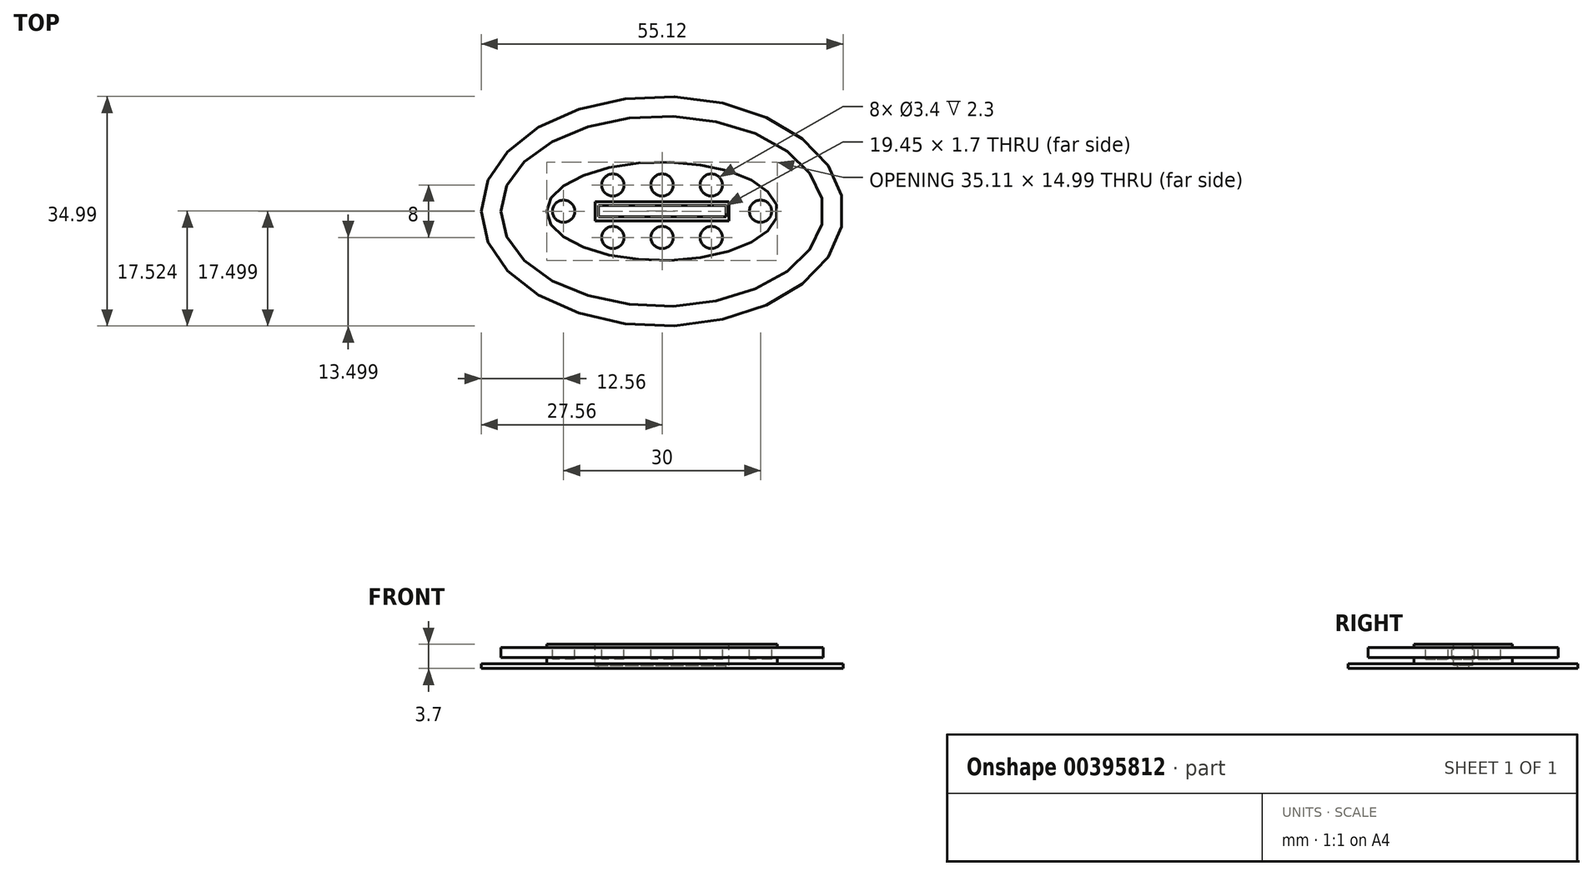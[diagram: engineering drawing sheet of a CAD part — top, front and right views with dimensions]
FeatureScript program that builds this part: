
annotation { "Feature Type Name" : "Feature", "Feature Type Description" : "" }
export const myFeature = defineFeature(function(context is Context, id is Id, definition is map)
    precondition{}
    {
        {
            var Q0;
            Q0=qCreatedBy(makeId("Top.planeOp"),FACE);
            var sketch = newSketch(context, id + "F0", { "sketchPlane" : qUnion([Q0])});
            skPoint(sketch, "E0", {"position": v(0, 39.46) * mm});
            skEllipse(sketch, "E1", {"center": v(0, 39.46) * mm, "majorRadius": 17.56 * mm, "minorRadius": 7.5 * mm, "majorAxis": v(-1, 0)});
            skSolve(sketch);
        }
        {
            var Q0;
            Q0 = qSketchRegion(id + "F0", true);
            var Q1;
            Q1 = qSketchRegion(id + "F2", true);
            extrude(context, id + "F1", {"entities" : qUnion([Q0, Q1]), "oppositeDirection" : true, "offsetDistance" : 25 * mm, "depth" : 2 * mm});
        }
        {
            var Q0;
            Q0=makeQuery(id+"F1.opExtrude","CAP_FACE",FACE,{"disambiguationData":[OSD([sQuery(id+"F0.wireOp",EDGE,"E1")])],"isStart":true});
            var sketch = newSketch(context, id + "F2", { "sketchPlane" : qUnion([Q0])});
            skPoint(sketch, "E2", {"position": v(0, 39.46) * mm});
            skEllipse(sketch, "E3", {"center": v(0, 39.46) * mm, "majorRadius": 24.56 * mm, "minorRadius": 14.5 * mm, "majorAxis": v(-1, 0)});
            skPoint(sketch, "E4", {"position": v(-24.56, 39.46) * mm});
            skPoint(sketch, "E5", {"position": v(0, 53.95) * mm});
            skPoint(sketch, "E6", {"position": v(0, 24.96) * mm});
            skPoint(sketch, "E7", {"position": v(24.56, 39.46) * mm});
            skPoint(sketch, "E8", {"position": v(0, 46.95) * mm});
            skPoint(sketch, "E9", {"position": v(-17.56, 39.46) * mm});
            skPoint(sketch, "E10", {"position": v(0, 31.96) * mm});
            skPoint(sketch, "E11", {"position": v(17.56, 39.46) * mm});
            skSolve(sketch);
        }
        {
            var Q0;
            Q0 = qSketchRegion(id + "F2", true);
            extrude(context, id + "F3", {"entities" : qUnion([Q0]), "operationType" : NewBodyOperationType.ADD, "oppositeDirection" : true, "depth" : 0.5 * mm});
        }
        {
            var Q0;
            Q0=makeQuery(id+"F3.boolean.opBoolean","MERGE",FACE,{"derivedFrom":[makeQuery(id+"F1.opExtrude","CAP_FACE",FACE,{"disambiguationData":[OSD([sQuery(id+"F0.wireOp",EDGE,"E1")])],"isStart":true}),makeQuery(id+"F3.opExtrude","CAP_FACE",FACE,{"disambiguationData":[OSD([sQuery(id+"F2.wireOp",EDGE,"E3")])],"isStart":true})]});
            var sketch = newSketch(context, id + "F4", { "sketchPlane" : qUnion([Q0])});
            skPoint(sketch, "E12", {"position": v(0, 39.46) * mm});
            skEllipse(sketch, "E13", {"center": v(0, 39.46) * mm, "majorRadius": 17.56 * mm, "minorRadius": 7.5 * mm, "majorAxis": v(-1, 0)});
            skSolve(sketch);
        }
        {
            var Q0;
            Q0 = qSketchRegion(id + "F4", true);
            extrude(context, id + "F5", {"entities" : qUnion([Q0]), "operationType" : NewBodyOperationType.ADD, "depth" : 1.5 * mm});
        }
        {
            var Q0;
            Q0=makeQuery(id+"F5.opExtrude","CAP_FACE",FACE,{"disambiguationData":[OSD([sQuery(id+"F4.wireOp",EDGE,"E13")])],"isStart":false});
            var sketch = newSketch(context, id + "F6", { "sketchPlane" : qUnion([Q0])});
            skPoint(sketch, "E14", {"position": v(0, 39.46) * mm});
            skLineSegment(sketch, "E15.bottom", {"start": v(-10.2, 40.9) * mm, "end": v(10.2, 40.9) * mm});
            skLineSegment(sketch, "E15.top", {"start": v(-10.2, 38) * mm, "end": v(10.2, 38) * mm});
            skLineSegment(sketch, "E15.left", {"start": v(-10.2, 40.9) * mm, "end": v(-10.2, 38) * mm});
            skLineSegment(sketch, "E15.right", {"start": v(10.2, 40.9) * mm, "end": v(10.2, 38) * mm});
            skSolve(sketch);
        }
        {
            var Q0;
            Q0=makeQuery(id+"F5.opExtrude","CAP_FACE",FACE,{"disambiguationData":[OSD([sQuery(id+"F4.wireOp",EDGE,"E13")])],"isStart":false});
            var sketch = newSketch(context, id + "F7", { "sketchPlane" : qUnion([Q0])});
            skPoint(sketch, "E16", {"position": v(0, 39.46) * mm});
            skPoint(sketch, "E17", {"position": v(-15, 39.46) * mm});
            skPoint(sketch, "E18", {"position": v(0, 43.46) * mm});
            skPoint(sketch, "E19", {"position": v(0, 35.46) * mm});
            skPoint(sketch, "E20", {"position": v(15, 39.46) * mm});
            skCircle(sketch, "E21", {"center": v(-15, 39.46) * mm, "radius": 1.7 * mm});
            skCircle(sketch, "E22", {"center": v(0, 43.46) * mm, "radius": 1.7 * mm});
            skCircle(sketch, "E23", {"center": v(15, 39.46) * mm, "radius": 1.7 * mm});
            skCircle(sketch, "E24", {"center": v(0, 35.46) * mm, "radius": 1.7 * mm});
            skPoint(sketch, "E25", {"position": v(-7.5, 43.46) * mm});
            skPoint(sketch, "E26", {"position": v(7.5, 43.46) * mm});
            skPoint(sketch, "E27", {"position": v(7.5, 35.46) * mm});
            skPoint(sketch, "E28", {"position": v(-7.5, 35.46) * mm});
            skCircle(sketch, "E29", {"center": v(-7.5, 35.46) * mm, "radius": 1.7 * mm});
            skCircle(sketch, "E30", {"center": v(-7.5, 43.46) * mm, "radius": 1.7 * mm});
            skCircle(sketch, "E31", {"center": v(7.5, 43.46) * mm, "radius": 1.7 * mm});
            skCircle(sketch, "E32", {"center": v(7.5, 35.46) * mm, "radius": 1.7 * mm});
            skSolve(sketch);
        }
        {
            var Q0;
            Q0 = qSketchRegion(id + "F7", true);
            extrude(context, id + "F8", {"entities" : qUnion([Q0]), "operationType" : NewBodyOperationType.REMOVE, "oppositeDirection" : true, "depth" : 2.3 * mm});
        }
        {
            var Q0;
            Q0=makeQuery(id+"F1.opExtrude","CAP_FACE",FACE,{"disambiguationData":[OSD([sQuery(id+"F0.wireOp",EDGE,"E1")])],"isStart":false});
            var sketch = newSketch(context, id + "F9", { "sketchPlane" : qUnion([Q0])});
            skPoint(sketch, "E33", {"position": v(0, -39.46) * mm});
            skEllipse(sketch, "E34", {"center": v(0, -39.46) * mm, "majorRadius": 27.56 * mm, "minorRadius": 17.5 * mm, "majorAxis": v(-1, 0)});
            skPoint(sketch, "E35", {"position": v(-17.56, -39.46) * mm});
            skPoint(sketch, "E36", {"position": v(0, -31.96) * mm});
            skPoint(sketch, "E37.positionSnap0", {"position": v(17.56, -39.46) * mm});
            skPoint(sketch, "E38", {"position": v(0, -46.95) * mm});
            skPoint(sketch, "E39", {"position": v(-27.56, -39.46) * mm});
            skPoint(sketch, "E40", {"position": v(0, -21.96) * mm});
            skPoint(sketch, "E41", {"position": v(27.56, -39.46) * mm});
            skPoint(sketch, "E42", {"position": v(0, -56.95) * mm});
            skSolve(sketch);
        }
        {
            var Q0;
            Q0 = qSketchRegion(id + "F9", true);
            extrude(context, id + "F10", {"entities" : qUnion([Q0]), "operationType" : NewBodyOperationType.ADD, "oppositeDirection" : true, "depth" : 0.5 * mm});
        }
        {
            var Q0;
            Q0=makeQuery(id+"F10.boolean.opBoolean","MERGE",FACE,{"derivedFrom":[makeQuery(id+"F1.opExtrude","CAP_FACE",FACE,{"disambiguationData":[OSD([sQuery(id+"F0.wireOp",EDGE,"E1")])],"isStart":false}),makeQuery(id+"F10.opExtrude","CAP_FACE",FACE,{"disambiguationData":[OSD([sQuery(id+"F9.wireOp",EDGE,"E34")])],"isStart":true})]});
            var sketch = newSketch(context, id + "F11", { "sketchPlane" : qUnion([Q0])});
            skPoint(sketch, "E43", {"position": v(0, -39.46) * mm});
            skPoint(sketch, "E44", {"position": v(0, -56.95) * mm});
            skPoint(sketch, "E45", {"position": v(-27.56, -39.46) * mm});
            skPoint(sketch, "E46", {"position": v(0, -21.96) * mm});
            skPoint(sketch, "E47", {"position": v(27.56, -39.46) * mm});
            skEllipse(sketch, "E48", {"center": v(0, -39.46) * mm, "majorRadius": 17.56 * mm, "minorRadius": 7.5 * mm, "majorAxis": v(-1, 0)});
            skPoint(sketch, "E49", {"position": v(-17.56, -39.46) * mm});
            skPoint(sketch, "E50", {"position": v(0, -31.96) * mm});
            skPoint(sketch, "E51", {"position": v(17.56, -39.46) * mm});
            skPoint(sketch, "E52", {"position": v(0, -46.95) * mm});
            skSolve(sketch);
        }
        {
            var Q0;
            Q0 = qSketchRegion(id + "F11", true);
            extrude(context, id + "F12", {"entities" : qUnion([Q0]), "operationType" : NewBodyOperationType.ADD, "depth" : 0.2 * mm});
        }
        {
            var Q0;
            Q0=makeQuery(id+"F6.imprint","IMPRINT",FACE,{"disambiguationData":[TD([[makeQuery(id+"F6.imprint","IMPRINT",EDGE,{"derivedFrom":sQuery(id+"F6.wireOp",EDGE,"E15.bottom")}),-1.0]])]});
            extrude(context, id + "F13", {"entities" : qUnion([Q0]), "operationType" : NewBodyOperationType.REMOVE, "oppositeDirection" : true, "depth" : 3.2 * mm});
        }
        {
            var Q0;
            Q0=makeQuery(id+"F13.boolean.opBoolean","COPY",FACE,{"derivedFrom":makeQuery(id+"F13.opExtrude","CAP_FACE",FACE,{"disambiguationData":[OSD([sQuery(id+"F6.wireOp",EDGE,"E15.bottom"),sQuery(id+"F6.wireOp",EDGE,"E15.top"),sQuery(id+"F6.wireOp",EDGE,"E15.left"),sQuery(id+"F6.wireOp",EDGE,"E15.right")])],"isStart":false})});
            var sketch = newSketch(context, id + "F14", { "sketchPlane" : qUnion([Q0])});
            skPoint(sketch, "E53", {"position": v(0, 39.48) * mm});
            skPoint(sketch, "E54", {"position": v(0, 40.9) * mm});
            skPoint(sketch, "E55", {"position": v(0, 38) * mm});
            skPoint(sketch, "E56", {"position": v(10.2, 39.48) * mm});
            skPoint(sketch, "E57", {"position": v(-10.2, 39.48) * mm});
            skLineSegment(sketch, "E58.bottom", {"start": v(-9.72, 40.33) * mm, "end": v(9.72, 40.33) * mm});
            skLineSegment(sketch, "E58.top", {"start": v(-9.72, 38.63) * mm, "end": v(9.72, 38.63) * mm});
            skLineSegment(sketch, "E58.left", {"start": v(-9.72, 40.33) * mm, "end": v(-9.72, 38.63) * mm});
            skLineSegment(sketch, "E58.right", {"start": v(9.72, 40.33) * mm, "end": v(9.72, 38.63) * mm});
            skSolve(sketch);
        }
        {
            var Q0;
            Q0 = qSketchRegion(id + "F14", true);
            extrude(context, id + "F15", {"entities" : qUnion([Q0]), "operationType" : NewBodyOperationType.REMOVE, "oppositeDirection" : true, "depth" : 1 * mm});
        }
        {
            var Q0;
            Q0=makeQuery(id+"F3.boolean.opBoolean","MERGE",FACE,{"derivedFrom":[makeQuery(id+"F1.opExtrude","CAP_FACE",FACE,{"disambiguationData":[OSD([sQuery(id+"F0.wireOp",EDGE,"E1")])],"isStart":true}),makeQuery(id+"F3.opExtrude","CAP_FACE",FACE,{"disambiguationData":[OSD([sQuery(id+"F2.wireOp",EDGE,"E3")])],"isStart":true})]});
            var sketch = newSketch(context, id + "F16", { "sketchPlane" : qUnion([Q0])});
            skSolve(sketch);
        }
        {
            var Q0;
            Q0 = qSketchRegion(id + "F16", true);
            var Q1;
            Q1=makeQuery(id+"F16.imprint","IMPRINT",FACE,{"disambiguationData":[TD([[makeQuery(id+"F16.imprint","IMPRINT",EDGE,{"derivedFrom":makeQuery(id+"F3.opExtrude","CAP_EDGE",EDGE,{"disambiguationData":[OSD([sQuery(id+"F2.wireOp",EDGE,"E3")])],"isStart":true})}),1.0]])]});
            extrude(context, id + "F17", {"entities" : qUnion([Q0, Q1]), "operationType" : NewBodyOperationType.ADD, "depth" : 1 * mm, "offsetDistance" : 25 * mm});
        }
        {
            var Q0;
            Q0=makeQuery(id+"F10.boolean.opBoolean","MERGE",FACE,{"derivedFrom":[makeQuery(id+"F1.opExtrude","CAP_FACE",FACE,{"disambiguationData":[OSD([sQuery(id+"F0.wireOp",EDGE,"E1")])],"isStart":false}),makeQuery(id+"F10.opExtrude","CAP_FACE",FACE,{"disambiguationData":[OSD([sQuery(id+"F9.wireOp",EDGE,"E34")])],"isStart":true})]});
            var sketch = newSketch(context, id + "F18", { "sketchPlane" : qUnion([Q0])});
            skSolve(sketch);
        }
        {
            var Q0;
            Q0 = qSketchRegion(id + "F18", true);
            var Q1;
            Q1=makeQuery(id+"F18.imprint","IMPRINT",FACE,{"disambiguationData":[TD([[makeQuery(id+"F18.imprint","IMPRINT",EDGE,{"derivedFrom":makeQuery(id+"F10.opExtrude","CAP_EDGE",EDGE,{"disambiguationData":[OSD([sQuery(id+"F9.wireOp",EDGE,"E34")])],"isStart":true})}),1.0]])]});
            extrude(context, id + "F19", {"entities" : qUnion([Q0, Q1]), "operationType" : NewBodyOperationType.ADD, "depth" : 0.2 * mm, "offsetDistance" : 25 * mm});
        }
    });
